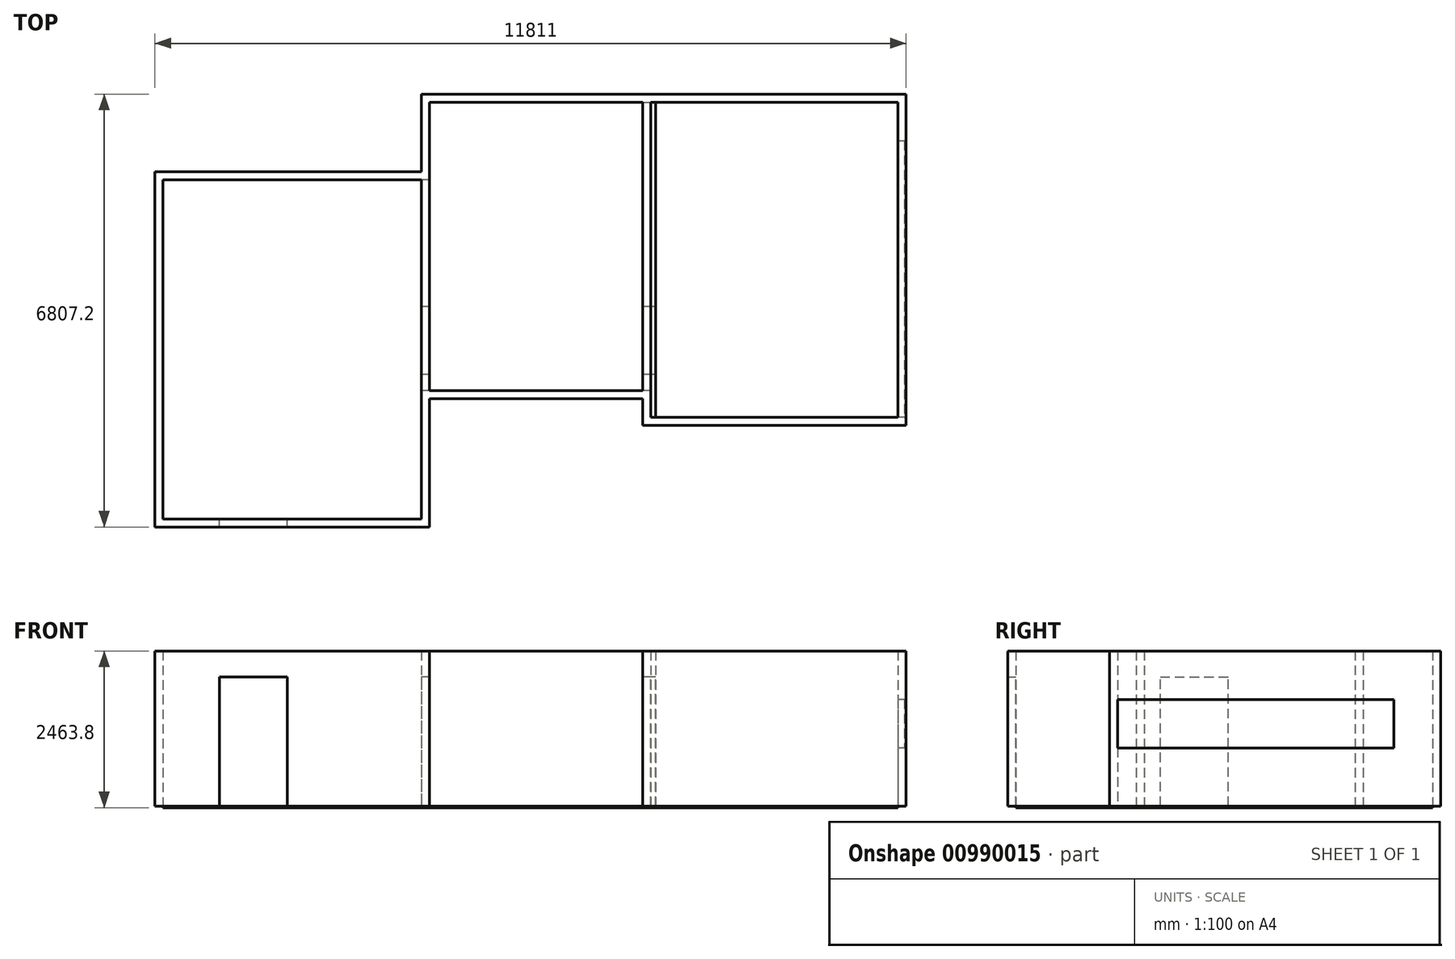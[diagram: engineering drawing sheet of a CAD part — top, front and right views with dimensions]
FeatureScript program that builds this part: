
annotation { "Feature Type Name" : "Feature", "Feature Type Description" : "" }
export const myFeature = defineFeature(function(context is Context, id is Id, definition is map)
    precondition{}
    {
        {
            var Q0;
            Q0=qCreatedBy(makeId("Top.planeOp"),FACE);
            var sketch = newSketch(context, id + "F0", { "sketchPlane" : qUnion([Q0])});
            skLineSegment(sketch, "E0.bottom", {"start": v(380.9, 2754.52) * mm, "end": v(4267.1, 2754.52) * mm});
            skLineSegment(sketch, "E0.top", {"start": v(380.9, -2198.48) * mm, "end": v(4267.1, -2198.48) * mm});
            skLineSegment(sketch, "E0.right", {"start": v(4267.1, 2754.52) * mm, "end": v(4267.1, -2198.48) * mm});
            skLineSegment(sketch, "E1.bottom", {"start": v(380.9, 2754.52) * mm, "end": v(-3098.9, 2754.52) * mm});
            skLineSegment(sketch, "E1.top", {"start": v(380.9, -1784.58) * mm, "end": v(-3225.9, -1784.58) * mm});
            skLineSegment(sketch, "E2.bottom", {"start": v(-3098.9, 1535.32) * mm, "end": v(-7289.9, 1535.32) * mm});
            skLineSegment(sketch, "E2.top", {"start": v(-3225.9, -3798.68) * mm, "end": v(-7289.9, -3798.68) * mm});
            skLineSegment(sketch, "E2.right", {"start": v(-7289.9, 1535.32) * mm, "end": v(-7289.9, -3798.68) * mm});
            skLineSegment(sketch, "E3", {"start": v(380.9, -1784.58) * mm, "end": v(380.9, -2198.48) * mm});
            skLineSegment(sketch, "E4", {"start": v(-3098.9, 2754.52) * mm, "end": v(-3098.9, 1535.32) * mm});
            skLineSegment(sketch, "E5", {"start": v(-3225.9, -3798.68) * mm, "end": v(-3225.9, -1784.58) * mm});
            skSolve(sketch);
        }
        {
            var Q0;
            Q0 = qSketchRegion(id + "F0", true);
            extrude(context, id + "F1", {"entities" : qUnion([Q0]), "depth" : 25.4 * mm, "offsetDistance" : 25.4 * mm});
        }
        {
            var Q0;
            Q0=makeQuery(id+"F1.opExtrude","CAP_FACE",FACE,{"disambiguationData":[OSD([sQuery(id+"F0.wireOp",EDGE,"E0.bottom"),sQuery(id+"F0.wireOp",EDGE,"E0.top"),sQuery(id+"F0.wireOp",EDGE,"E0.right"),sQuery(id+"F0.wireOp",EDGE,"E1.bottom"),sQuery(id+"F0.wireOp",EDGE,"E1.top"),sQuery(id+"F0.wireOp",EDGE,"E2.bottom"),sQuery(id+"F0.wireOp",EDGE,"E2.top"),sQuery(id+"F0.wireOp",EDGE,"E2.right"),sQuery(id+"F0.wireOp",EDGE,"E3"),sQuery(id+"F0.wireOp",EDGE,"E4"),sQuery(id+"F0.wireOp",EDGE,"E5")])],"isStart":false});
            var sketch = newSketch(context, id + "F2", { "sketchPlane" : qUnion([Q0])});
            skLineSegment(sketch, "E6.bottom", {"start": v(380.9, -2198.48) * mm, "end": v(4394.1, -2198.48) * mm});
            skLineSegment(sketch, "E6.top", {"start": v(380.9, -2325.48) * mm, "end": v(4394.1, -2325.48) * mm});
            skLineSegment(sketch, "E6.left", {"start": v(380.9, -2198.48) * mm, "end": v(380.9, -2325.48) * mm});
            skLineSegment(sketch, "E6.right", {"start": v(4394.1, -2198.48) * mm, "end": v(4394.1, -2325.48) * mm});
            skLineSegment(sketch, "E7.bottom", {"start": v(4267.1, 2754.52) * mm, "end": v(4394.1, 2754.52) * mm});
            skLineSegment(sketch, "E7.top", {"start": v(4267.1, -2325.48) * mm, "end": v(4394.1, -2325.48) * mm});
            skLineSegment(sketch, "E7.left", {"start": v(4267.1, 2754.52) * mm, "end": v(4267.1, -2325.48) * mm});
            skLineSegment(sketch, "E7.right", {"start": v(4394.1, 2754.52) * mm, "end": v(4394.1, -2325.48) * mm});
            skLineSegment(sketch, "E8.bottom", {"start": v(-3098.9, 2754.52) * mm, "end": v(4394.1, 2754.52) * mm});
            skLineSegment(sketch, "E8.top", {"start": v(-3098.9, 2881.52) * mm, "end": v(4394.1, 2881.52) * mm});
            skLineSegment(sketch, "E8.left", {"start": v(-3098.9, 2754.52) * mm, "end": v(-3098.9, 2881.52) * mm});
            skLineSegment(sketch, "E8.right", {"start": v(4394.1, 2754.52) * mm, "end": v(4394.1, 2881.52) * mm});
            skLineSegment(sketch, "E9.top", {"start": v(-3098.9, 2881.52) * mm, "end": v(-3225.9, 2881.52) * mm});
            skLineSegment(sketch, "E9.left", {"start": v(-3098.9, 1535.32) * mm, "end": v(-3098.9, 2881.52) * mm});
            skLineSegment(sketch, "E9.right", {"start": v(-3225.9, 1535.32) * mm, "end": v(-3225.9, 2881.52) * mm});
            skLineSegment(sketch, "E10.left", {"start": v(-7289.9, 1535.32) * mm, "end": v(-7289.9, 1662.32) * mm});
            skLineSegment(sketch, "E10.right", {"start": v(-3098.9, 1535.32) * mm, "end": v(-3098.9, 1662.32) * mm});
            skLineSegment(sketch, "E11.bottom", {"start": v(-7289.9, -3798.68) * mm, "end": v(-7416.9, -3798.68) * mm});
            skLineSegment(sketch, "E11.top", {"start": v(-7289.9, 1662.32) * mm, "end": v(-7416.9, 1662.32) * mm});
            skLineSegment(sketch, "E11.left", {"start": v(-7289.9, -3798.68) * mm, "end": v(-7289.9, 1662.32) * mm});
            skLineSegment(sketch, "E11.right", {"start": v(-7416.9, -3798.68) * mm, "end": v(-7416.9, 1662.32) * mm});
            skLineSegment(sketch, "E12.bottom", {"start": v(-7416.9, -3798.68) * mm, "end": v(-3225.9, -3798.68) * mm});
            skLineSegment(sketch, "E12.top", {"start": v(-7416.9, -3925.68) * mm, "end": v(-3225.9, -3925.68) * mm});
            skLineSegment(sketch, "E12.left", {"start": v(-7416.9, -3798.68) * mm, "end": v(-7416.9, -3925.68) * mm});
            skLineSegment(sketch, "E12.right", {"start": v(-3225.9, -3798.68) * mm, "end": v(-3225.9, -3925.68) * mm});
            skLineSegment(sketch, "E13.bottom", {"start": v(-3225.9, -1784.58) * mm, "end": v(-3098.9, -1784.58) * mm});
            skLineSegment(sketch, "E13.top", {"start": v(-3225.9, -3925.68) * mm, "end": v(-3098.9, -3925.68) * mm});
            skLineSegment(sketch, "E14.right", {"start": v(380.9, -1784.58) * mm, "end": v(380.9, -1991.53) * mm});
            skLineSegment(sketch, "E15.bottom", {"start": v(380.9, -2325.48) * mm, "end": v(253.9, -2325.48) * mm});
            skLineSegment(sketch, "E15.left", {"start": v(380.9, -2325.48) * mm, "end": v(380.9, -1784.58) * mm});
            skLineSegment(sketch, "E16.left", {"start": v(-3225.9, -1784.58) * mm, "end": v(-3225.9, -1991.53) * mm});
            skLineSegment(sketch, "E17", {"start": v(253.9, -2325.48) * mm, "end": v(253.9, -1911.58) * mm});
            skLineSegment(sketch, "E18", {"start": v(253.9, -1911.58) * mm, "end": v(-3098.9, -1911.58) * mm});
            skLineSegment(sketch, "E19", {"start": v(-3098.9, -1911.58) * mm, "end": v(-3098.9, -3925.68) * mm});
            skLineSegment(sketch, "E20.top", {"start": v(380.9, 2754.52) * mm, "end": v(253.9, 2754.52) * mm});
            skLineSegment(sketch, "E20.left", {"start": v(380.9, -1784.58) * mm, "end": v(380.9, 2754.52) * mm});
            skLineSegment(sketch, "E20.right", {"start": v(253.9, -1784.58) * mm, "end": v(253.9, 2754.52) * mm});
            skLineSegment(sketch, "E21.left", {"start": v(-3098.9, 1535.32) * mm, "end": v(-3098.9, -1784.58) * mm});
            skLineSegment(sketch, "E21.right", {"start": v(-3225.9, 1535.32) * mm, "end": v(-3225.9, -1784.58) * mm});
            skLineSegment(sketch, "E22", {"start": v(253.9, -1784.58) * mm, "end": v(-3098.9, -1784.58) * mm});
            skLineSegment(sketch, "E23", {"start": v(-3225.9, 1535.32) * mm, "end": v(-7289.9, 1535.32) * mm});
            skLineSegment(sketch, "E24", {"start": v(-3225.9, 1662.32) * mm, "end": v(-7289.9, 1662.32) * mm});
            skLineSegment(sketch, "E25", {"start": v(-3225.9, -1991.53) * mm, "end": v(-3225.9, -3798.68) * mm});
            skSolve(sketch);
        }
        {
            var Q0;
            Q0 = qSketchRegion(id + "F2", true);
            extrude(context, id + "F3", {"entities" : qUnion([Q0]), "depth" : 2438.4 * mm, "offsetDistance" : 25.4 * mm});
        }
        {
            var Q0;
            Q0=makeQuery(id+"F3.opExtrude","SWEPT_FACE",FACE,{"disambiguationData":[OSD([sQuery(id+"F2.wireOp",EDGE,"E20.right")])]});
            var sketch = newSketch(context, id + "F4", { "sketchPlane" : qUnion([Q0])});
            skLineSegment(sketch, "E26.bottom", {"start": v(1530.58, 25.4) * mm, "end": v(463.78, 25.4) * mm});
            skLineSegment(sketch, "E26.top", {"start": v(1530.58, 2057.4) * mm, "end": v(463.78, 2057.4) * mm});
            skLineSegment(sketch, "E26.left", {"start": v(1530.58, 25.4) * mm, "end": v(1530.58, 2057.4) * mm});
            skLineSegment(sketch, "E26.right", {"start": v(463.78, 25.4) * mm, "end": v(463.78, 2057.4) * mm});
            skSolve(sketch);
        }
        {
            var Q0;
            Q0 = qSketchRegion(id + "F4", true);
            extrude(context, id + "F5", {"entities" : qUnion([Q0]), "operationType" : NewBodyOperationType.REMOVE, "oppositeDirection" : true, "depth" : 127 * mm, "offsetDistance" : 25.4 * mm, "hasSecondDirection" : true, "secondDirectionOppositeDirection" : false, "secondDirectionDepth" : 3530.6 * mm});
        }
        {
            var Q0;
            Q0=makeQuery(id+"F3.opExtrude","SWEPT_FACE",FACE,{"disambiguationData":[OSD([sQuery(id+"F2.wireOp",EDGE,"E12.bottom")])]});
            var sketch = newSketch(context, id + "F6", { "sketchPlane" : qUnion([Q0])});
            skLineSegment(sketch, "E27.bottom", {"start": v(5334.1, 25.4) * mm, "end": v(6400.9, 25.4) * mm});
            skLineSegment(sketch, "E27.top", {"start": v(5334.1, 2057.4) * mm, "end": v(6400.9, 2057.4) * mm});
            skLineSegment(sketch, "E27.left", {"start": v(5334.1, 25.4) * mm, "end": v(5334.1, 2057.4) * mm});
            skLineSegment(sketch, "E27.right", {"start": v(6400.9, 25.4) * mm, "end": v(6400.9, 2057.4) * mm});
            skSolve(sketch);
        }
        {
            var Q0;
            Q0 = qSketchRegion(id + "F6", true);
            extrude(context, id + "F7", {"entities" : qUnion([Q0]), "operationType" : NewBodyOperationType.REMOVE, "oppositeDirection" : true, "depth" : 127 * mm, "offsetDistance" : 25.4 * mm});
        }
        {
            var Q0;
            Q0=makeQuery(id+"F3.opExtrude","SWEPT_FACE",FACE,{"disambiguationData":[OSD([sQuery(id+"F2.wireOp",EDGE,"E7.left")])]});
            var sketch = newSketch(context, id + "F8", { "sketchPlane" : qUnion([Q0])});
            skLineSegment(sketch, "E28.bottom", {"start": v(-2144.92, 1701.8) * mm, "end": v(2198.48, 1701.8) * mm});
            skLineSegment(sketch, "E28.top", {"start": v(-2144.92, 939.8) * mm, "end": v(2198.48, 939.8) * mm});
            skLineSegment(sketch, "E28.left", {"start": v(-2144.92, 1701.8) * mm, "end": v(-2144.92, 939.8) * mm});
            skLineSegment(sketch, "E28.right", {"start": v(2198.48, 1701.8) * mm, "end": v(2198.48, 939.8) * mm});
            skSolve(sketch);
        }
        {
            var Q0;
            Q0 = qSketchRegion(id + "F8", true);
            extrude(context, id + "F9", {"entities" : qUnion([Q0]), "operationType" : NewBodyOperationType.REMOVE, "oppositeDirection" : true, "depth" : 127 * mm, "offsetDistance" : 25.4 * mm});
        }
        {
            var Q0;
            Q0=makeQuery(id+"F3.opExtrude","SWEPT_FACE",FACE,{"disambiguationData":[OSD([sQuery(id+"F2.wireOp",EDGE,"E7.right"),sQuery(id+"F2.wireOp",EDGE,"E8.right")])]});
            var sketch = newSketch(context, id + "F10", { "sketchPlane" : qUnion([Q0])});
            skLineSegment(sketch, "E29.bottom", {"start": v(2144.92, 1701.8) * mm, "end": v(-2198.48, 1701.8) * mm});
            skLineSegment(sketch, "E29.top", {"start": v(2144.92, 939.8) * mm, "end": v(-2198.48, 939.8) * mm});
            skLineSegment(sketch, "E29.left", {"start": v(2144.92, 1701.8) * mm, "end": v(2144.92, 939.8) * mm});
            skLineSegment(sketch, "E29.right", {"start": v(-2198.48, 1701.8) * mm, "end": v(-2198.48, 939.8) * mm});
            skSolve(sketch);
        }
        {
            var Q0;
            Q0 = qSketchRegion(id + "F10", true);
            extrude(context, id + "F11", {"entities" : qUnion([Q0]), "oppositeDirection" : true, "depth" : 25.4 * mm, "offsetDistance" : 25.4 * mm});
        }
        {
            var Q0;
            Q0=makeQuery(id+"F1.opExtrude","CAP_FACE",FACE,{"disambiguationData":[OSD([sQuery(id+"F0.wireOp",EDGE,"E0.bottom"),sQuery(id+"F0.wireOp",EDGE,"E0.top"),sQuery(id+"F0.wireOp",EDGE,"E0.right"),sQuery(id+"F0.wireOp",EDGE,"E1.bottom"),sQuery(id+"F0.wireOp",EDGE,"E1.top"),sQuery(id+"F0.wireOp",EDGE,"E2.bottom"),sQuery(id+"F0.wireOp",EDGE,"E2.top"),sQuery(id+"F0.wireOp",EDGE,"E2.right"),sQuery(id+"F0.wireOp",EDGE,"E3"),sQuery(id+"F0.wireOp",EDGE,"E4"),sQuery(id+"F0.wireOp",EDGE,"E5")])],"isStart":false});
            var sketch = newSketch(context, id + "F12", { "sketchPlane" : qUnion([Q0])});
            skLineSegment(sketch, "E30", {"start": v(380.9, 2754.52) * mm, "end": v(2031.9, 2754.52) * mm});
            skLineSegment(sketch, "E31", {"start": v(380.9, 2754.52) * mm, "end": v(380.9, 595.52) * mm});
            skLineSegment(sketch, "E32", {"start": v(380.9, 595.52) * mm, "end": v(380.9, 290.72) * mm});
            skLineSegment(sketch, "E33", {"start": v(2031.9, 2754.52) * mm, "end": v(2336.7, 2754.52) * mm});
            skLineSegment(sketch, "E34", {"start": v(380.9, 290.72) * mm, "end": v(2336.7, 2754.52) * mm});
            skSolve(sketch);
        }
        {
            var Q0;
            Q0 = qSketchRegion(id + "F12", true);
            extrude(context, id + "F13", {"entities" : qUnion([Q0]), "depth" : 2438.4 * mm, "offsetDistance" : 25.4 * mm});
        }
        {
            var Q0;
            Q0=makeQuery(id+"F13.opExtrude","SWEPT_BODY",BODY,{"disambiguationData":[OSD([sQuery(id+"F12.wireOp",EDGE,"E30"),sQuery(id+"F12.wireOp",EDGE,"E31"),sQuery(id+"F12.wireOp",EDGE,"E32"),sQuery(id+"F12.wireOp",EDGE,"E33"),sQuery(id+"F12.wireOp",EDGE,"E34")])]});
            transform(context, id + "F14", {"entities" : qUnion([Q0]), "transformType" : TransformType.TRANSLATION_3D, "dx" : 0 * mm, "dy" : 0 * mm, "dz" : 0 * mm, "makeCopy" : true});
        }
        {
            var Q0;
            Q0=makeQuery(id+"F14.opPattern","COPY",BODY,{"derivedFrom":makeQuery(id+"F13.opExtrude","SWEPT_BODY",BODY,{"disambiguationData":[OSD([sQuery(id+"F12.wireOp",EDGE,"E30"),sQuery(id+"F12.wireOp",EDGE,"E31"),sQuery(id+"F12.wireOp",EDGE,"E32"),sQuery(id+"F12.wireOp",EDGE,"E33"),sQuery(id+"F12.wireOp",EDGE,"E34")])]}),"instanceName":"1"});
            deleteBodies(context, id + "F15", {"entities" : qUnion([Q0])});
        }
        {
            var Q0;
            Q0=makeQuery(id+"F13.opExtrude","SWEPT_BODY",BODY,{"disambiguationData":[OSD([sQuery(id+"F12.wireOp",EDGE,"E30"),sQuery(id+"F12.wireOp",EDGE,"E31"),sQuery(id+"F12.wireOp",EDGE,"E32"),sQuery(id+"F12.wireOp",EDGE,"E33"),sQuery(id+"F12.wireOp",EDGE,"E34")])]});
            deleteBodies(context, id + "F16", {"entities" : qUnion([Q0])});
        }
        {
            var Q0;
            Q0=makeQuery(id+"F3.opExtrude","SWEPT_FACE",FACE,{"disambiguationData":[OSD([sQuery(id+"F2.wireOp",EDGE,"E15.left"),sQuery(id+"F2.wireOp",EDGE,"E14.right"),sQuery(id+"F2.wireOp",EDGE,"E20.left")])]});
            var sketch = newSketch(context, id + "F17", { "sketchPlane" : qUnion([Q0])});
            skLineSegment(sketch, "E35", {"start": v(2754.52, 25.4) * mm, "end": v(2754.52, 2463.8) * mm});
            skLineSegment(sketch, "E36", {"start": v(2754.52, 2463.8) * mm, "end": v(-2198.48, 2463.8) * mm});
            skLineSegment(sketch, "E37", {"start": v(-2198.48, 2463.8) * mm, "end": v(-2198.48, 25.4) * mm});
            skLineSegment(sketch, "E38", {"start": v(-2198.48, 25.4) * mm, "end": v(-1530.58, 25.4) * mm});
            skLineSegment(sketch, "E39", {"start": v(-1530.58, 25.4) * mm, "end": v(-1530.58, 2057.4) * mm});
            skLineSegment(sketch, "E40", {"start": v(-1530.58, 2057.4) * mm, "end": v(-463.78, 2057.4) * mm});
            skLineSegment(sketch, "E41", {"start": v(-463.78, 2057.4) * mm, "end": v(-463.78, 25.4) * mm});
            skLineSegment(sketch, "E42", {"start": v(-463.78, 25.4) * mm, "end": v(2754.52, 25.4) * mm});
            skSolve(sketch);
        }
        {
            var Q0;
            Q0 = qSketchRegion(id + "F17", true);
            extrude(context, id + "F18", {"entities" : qUnion([Q0]), "depth" : 76.2 * mm, "offsetDistance" : 25.4 * mm});
        }
    });
